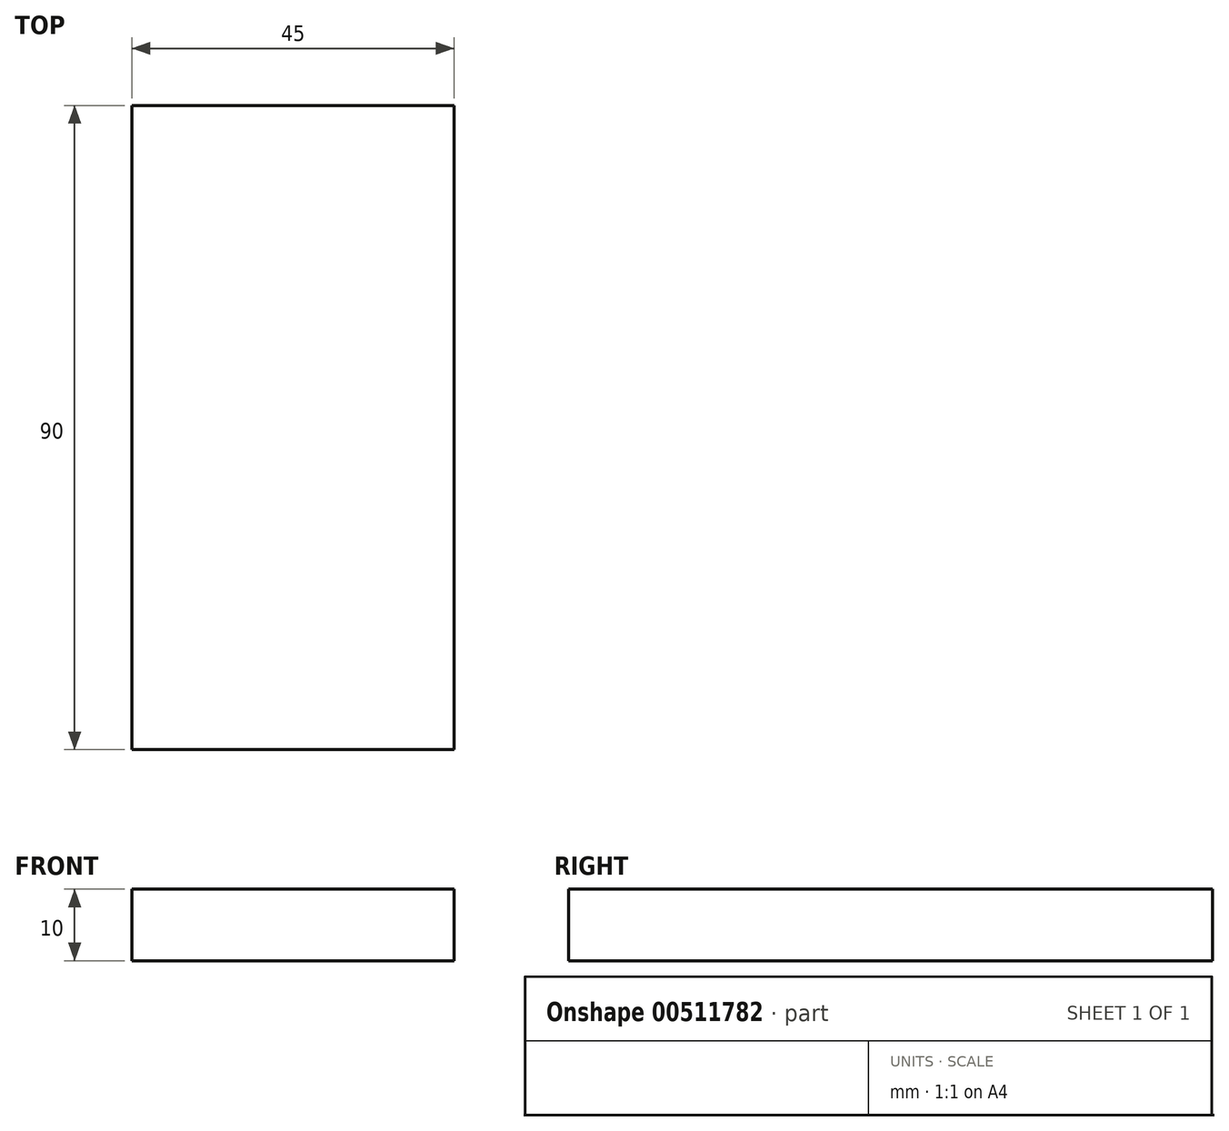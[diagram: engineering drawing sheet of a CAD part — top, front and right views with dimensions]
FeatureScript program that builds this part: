
annotation { "Feature Type Name" : "Feature", "Feature Type Description" : "" }
export const myFeature = defineFeature(function(context is Context, id is Id, definition is map)
    precondition{}
    {
        {
            var Q0;
            Q0=qCreatedBy(makeId("Top.planeOp"),FACE);
            var sketch = newSketch(context, id + "F0", { "sketchPlane" : qUnion([Q0])});
            skLineSegment(sketch, "E0.bottom", {"start": v(22.5, -45) * mm, "end": v(-22.5, -45) * mm});
            skLineSegment(sketch, "E0.top", {"start": v(22.5, 45) * mm, "end": v(-22.5, 45) * mm});
            skLineSegment(sketch, "E0.left", {"start": v(22.5, -45) * mm, "end": v(22.5, 45) * mm});
            skLineSegment(sketch, "E0.right", {"start": v(-22.5, -45) * mm, "end": v(-22.5, 45) * mm});
            skPoint(sketch, "E0.middle", {"position": v(0, 0) * mm});
            skSolve(sketch);
        }
        {
            var Q0;
            Q0 = qSketchRegion(id + "F0", true);
            extrude(context, id + "F1", {"entities" : qUnion([Q0]), "depth" : 10 * mm});
        }
    });
